# Revit family: Laser Range
name_source: partatom
category: Furniture
revit_build: Autodesk Revit 2018 (Build: 20170223_1515(x64)
units: mm (PartAtom-declared; Revit-internal decimal feet)

## family parameters
Always vertical = Yes
Cut with Voids When Loaded = No
OmniClass Number = 23.40.20.00
OmniClass Title = General Furniture and Specialties
Room Calculation Point = No
Shared = No
Work Plane-Based = No

## types (22) — shared parameters

## per-type parameters (varying)
| type | Furniture Type |
| Coffee Table - Oval (1000X600X400) | Laser Range : Cofee Table - Oval (1000X600X400) |
| Coffee Table - Square (750X750X400) | Laser Range : Coffee Table - Square (750X750X400) |
| Coffee Table - Round (800X800X400) | Laser Range : Coffee Table - Round (800X800X400) |
| Coffee Table - Rectangle (900X500X400) | Laser Range : Coffee Table - Rectangle (900X500X400) |
| Coffee Table - Rectangle (900X350X400) | Laser Range : Coffee Table - Rectangle (900X350X400) |
| Laptop Table (400X500X600) | Laser Range : Laptop Table (400X500X600) |
| Side Table - Oval Side (1000X600X600) | Laser Range : Side Table - Oval (1000X600X600) |
| Side Table - Square (750X750X600) | Laser Range : Side Table - Square (750X750X600) |
| Side Table - Round (800X800X600) | Laser Range : Side Table - Round (800X800X600) |
| Side Table - Rectangle (900X350X600) | Laser Range : Side Table - Rectangle (900X350X600) |
| Side Table - Rectangle (900X500X600) | Laser Range : Side Table - Rectangle (900X500X600) |
| Bistro Table - Square (750X750X730) | Laser Range : Bistro - Square (750X750X700) |
| Bistro Table - Round (800X800X730) | Laser Range : Bistro - Round (800X800X700) |
| Standing Height Square Table (750X750X1050) | Laser Range : Standing Height - Square (750X750X1050) |
| Standing Height Round Table (800X800X1050) | Laser Range : Standing Height - Round (800X800X1050) |
| Meeting Table - Square (1000X1000X730) | Laser Range : Meeting Table - Square (1000X1000X730) |
| Meeting Table - Round (1000X1000X730) | Laser Range : Meeting Table - Round (1000X1000X730) |
| Meeting Table - Round (1200X1200X730) | Laser Range : Meeting Table - Round (1200X1200X730) |
| Meeting Table - Round (1500X1500X730) | Laser Range : Meeting Table - Round (1500X1500X730) |
| Large Table - Oval (2000X1000X730) | Laser Range : Large Oval Table (2000X1000X730) |
| Large Table -  Rectangular (2200X1200X730) | Laser Range : Large Rectangular Table (2000X1000X730) |
| Boardroom Table (4000X1200X730) | Laser Range : Boardroom Table (4000X1200X730) |

## geometry (parser evidence)
native form markers: Sweep x27
no freeform markers — native parametric forms only
